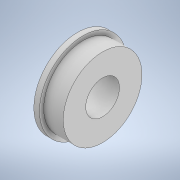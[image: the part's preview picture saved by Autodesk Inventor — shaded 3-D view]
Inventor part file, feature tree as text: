
AUTODESK INVENTOR PART (.ipt)
format: ipt  version: 2020 (Build 240168000, 168)  size: 136,704 bytes
history: native  units: in
note: dims shown in document units (in); Inventor stores cm internally (conversion verified against a paired STEP export)
features: revolve x1
ambient origin geometry x8: Origin, YZ Plane, XZ Plane, XY Plane, X Axis, Y Axis, Z Axis, Center Point
bodies: Solid1 (feature_tree)
feature tree (1):
  revolve  "Revolve1"  [1 undecoded]
note: 1 required parameter value undecoded (feature->parameter linkage not recoverable at this tier; creation-order binding heuristic only, values carry confidence <= 0.55)
